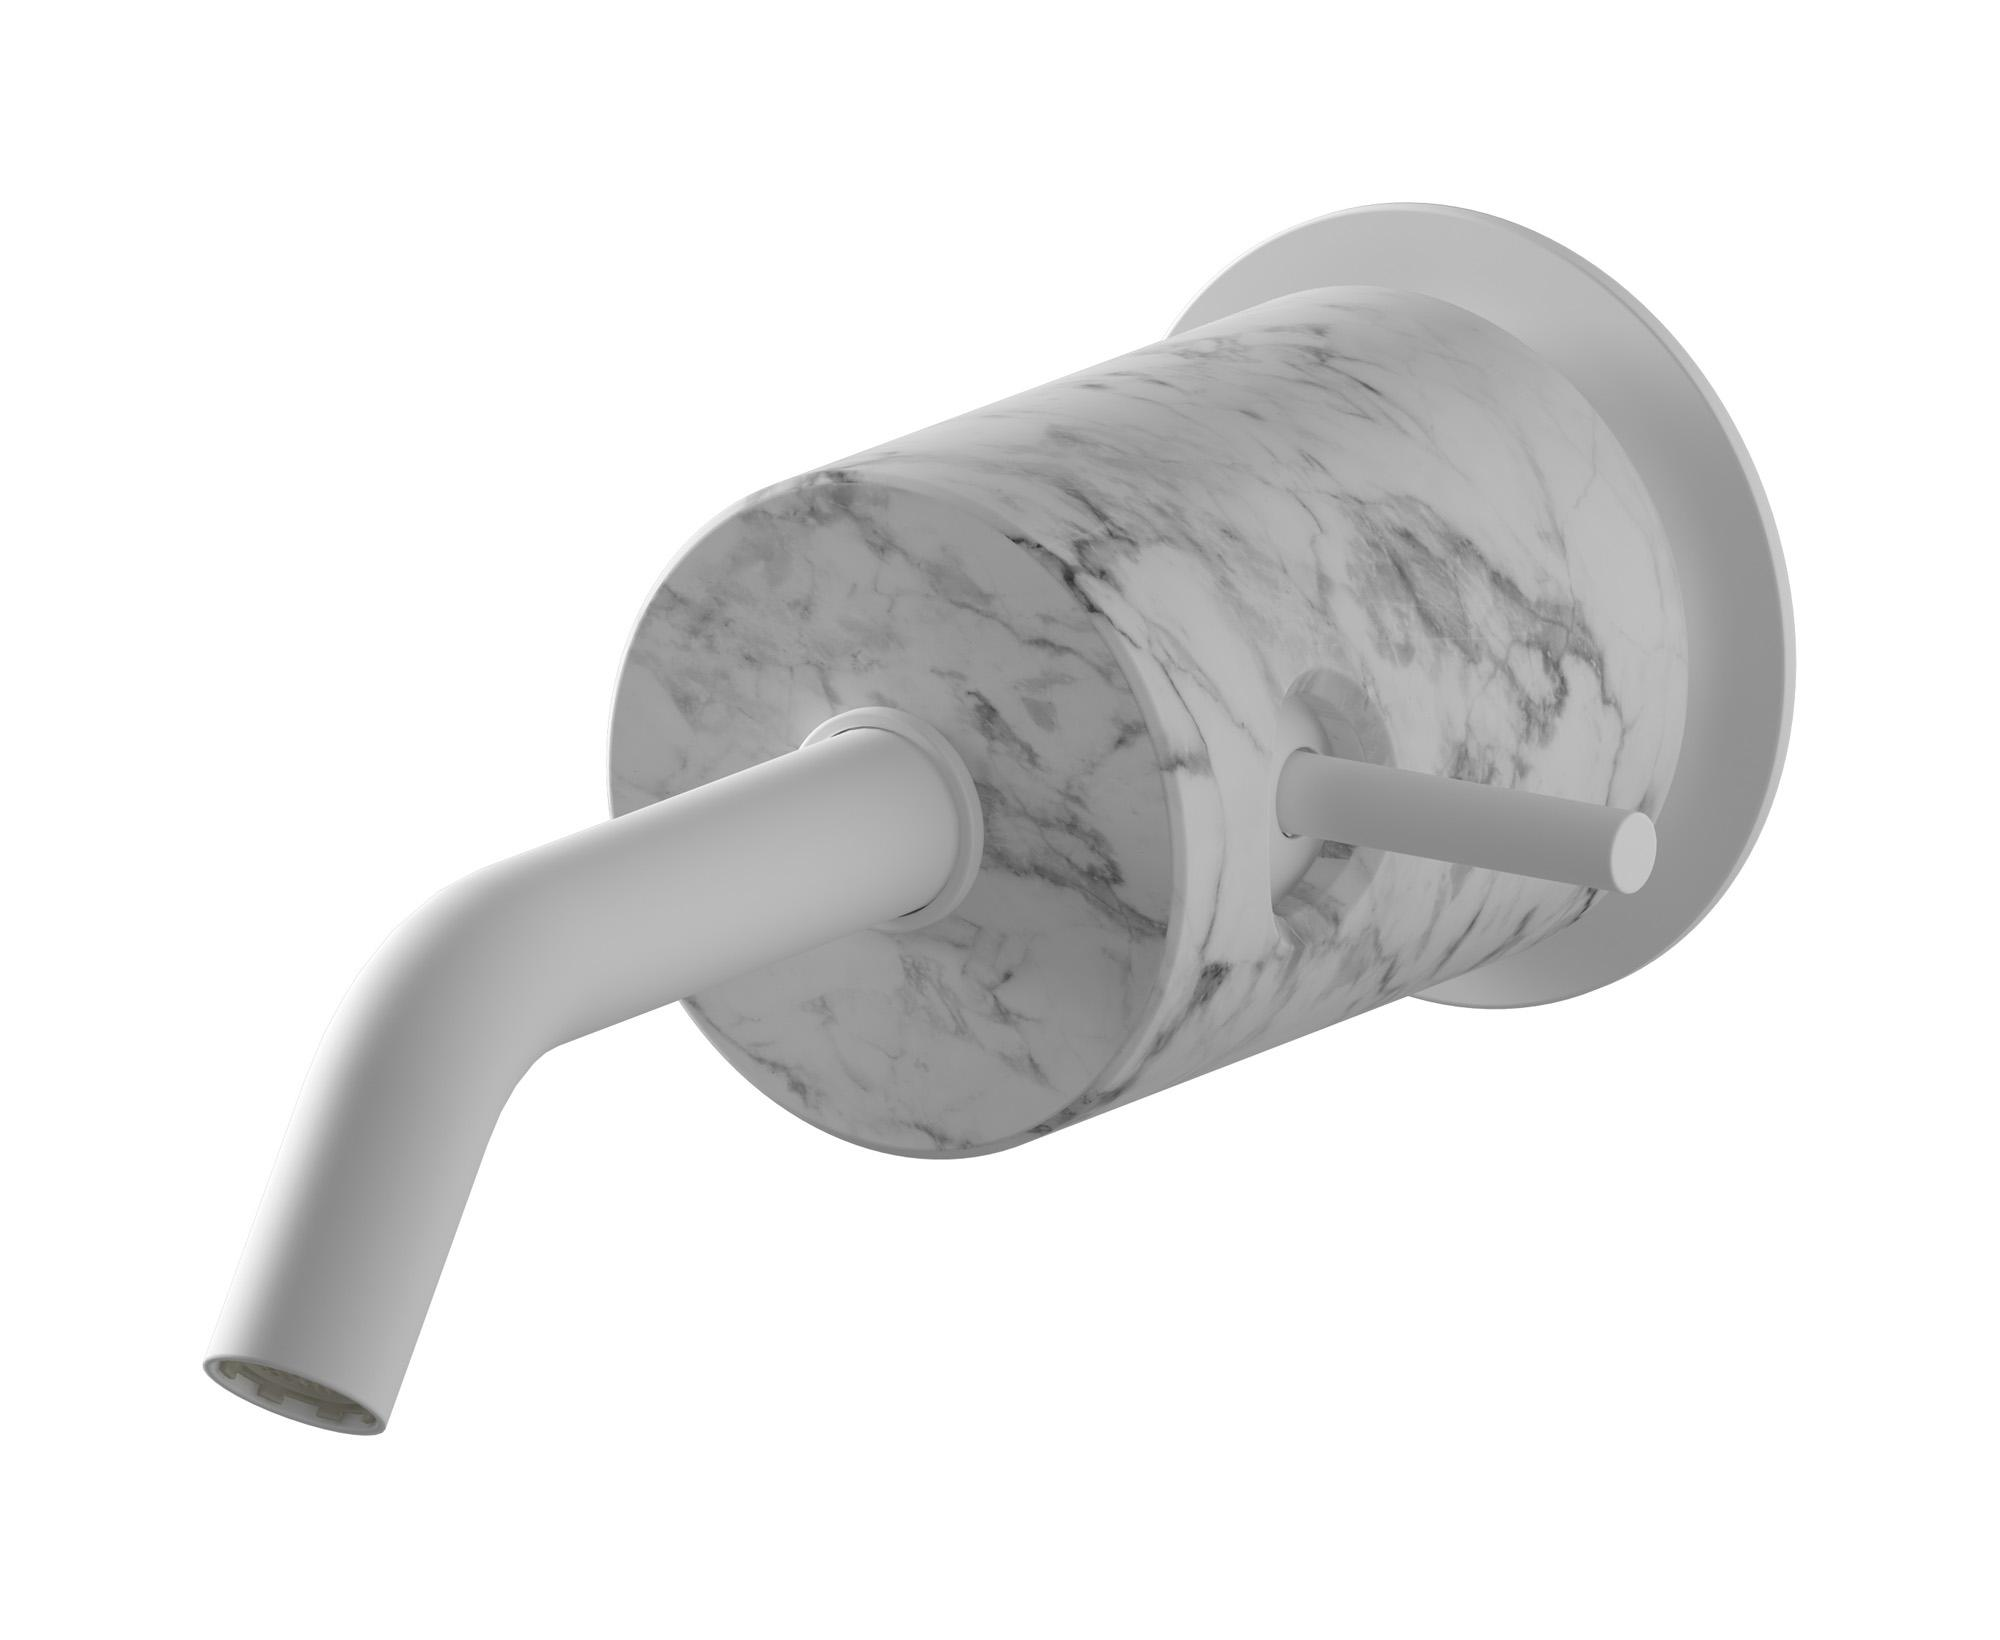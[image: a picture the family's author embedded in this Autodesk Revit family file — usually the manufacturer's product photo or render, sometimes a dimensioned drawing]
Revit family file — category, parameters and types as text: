
# Revit family: MR209_1
name_source: partatom
category: Apparecchi idraulici
units: mm (PartAtom-declared; Revit-internal decimal feet)

## family parameters
Basato su piano di lavoro = No
Condiviso = No
Mantieni orientamento annotazione = No
Numero OmniClass = 23.45.55.17
Punto di calcolo locali = No
Quota connettore circolare = Usa diametro
Sempre verticale = Sì
Taglio con vuoti quando caricato = No
Tipo di parte = Normale
Titolo OmniClass = Mixing Faucets

## types (14) — shared parameters
Cold water inlet = 10 mm  [stored 0.0328084 ft]
Commenti sul tipo = Washbasin mixer
Connessione CW = No
Connessione HW = No
Connessione di scarico = No
Connessione di ventilazione = No
Descrizione = Mono hole wall mounted washbasin mixer
Hot water inlet = 10 mm  [stored 0.0328084 ft]
Produttore = IB Rubinetterie S.p.A.
URL = https://www.weareib.it
zero-valued in all types: Prospetto di default

## per-type parameters (varying)
| type | Finishes surface | Immagine tipo | Modello |
| Chrome | IB_Chrome | MR209CC_1.jpg | MR209CC_1 |
| Platinum | IB_Platinum | MR209PL_1.jpg | MR209PL_1 |
| Brushed nickel | IB_Brushed nickel | MR209SS_1.jpg | MR209SS_1 |
| Natural brass | IB_Brass | MR209ON_1.jpg | MR209ON_1 |
| Matt white | IB_matt white | MR209BO_1.jpg | MR209BO_1 |
| Matt black | IB_matt black | MR209NP_1.jpg | MR209NP_1 |
| Black chrome | IB_Black chrome | MR209CF_1.jpg | MR209CF_1 |
| Brushed black chrome | IB_Brushed black chrome | MR209CS_1.jpg | MR209CS_1 |
| Pale gold | IB_Pale gold | MR209II_1.jpg | MR209II_1 |
| Brushed pale gold | IB_brushed pale gold | MR209IS_1.jpg | MR209IS_1 |
| Rose gold | IB_Rose gold | MR209RS_1.jpg | MR209RS_1 |
| Brushed rose gold | IB_Brushed rose gold | MR209SR_1.jpg | MR209SR_1 |
| Gold | IB_gold | MR209OO_1.jpg | MR209OO_1 |
| Brushed gold | IB_brushed gold | MR209OS_1.jpg | MR209OS_1 |

note: [stored X ft] marks values corroborated as IEEE doubles in the binary element streams (Revit-internal decimal feet)
